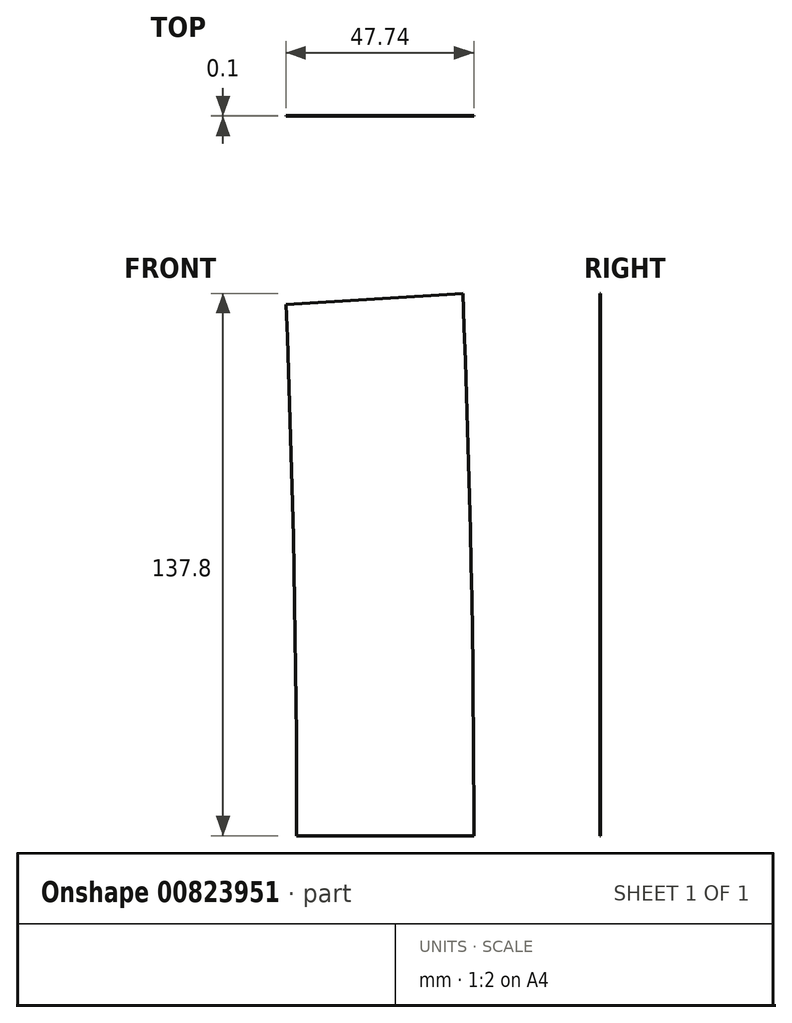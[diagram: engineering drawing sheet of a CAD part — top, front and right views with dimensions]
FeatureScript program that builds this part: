
annotation { "Feature Type Name" : "Feature", "Feature Type Description" : "" }
export const myFeature = defineFeature(function(context is Context, id is Id, definition is map)
    precondition{}
    {
        {
            var Q0;
            Q0=qCreatedBy(makeId("Front.planeOp"),FACE);
            var sketch = newSketch(context, id + "F0", { "sketchPlane" : qUnion([Q0])});
            skLineSegment(sketch, "E0", {"start": v(-45, 0) * mm, "end": v(0, 0) * mm});
            skLineSegment(sketch, "E1", {"start": v(-47.74, 134.96) * mm, "end": v(-2.83, 137.8) * mm});
            skArc(sketch, "E2", {"start": v(0, 0) * mm, "mid": v(-0.7, 68.92) * mm, "end": v(-2.83, 137.8) * mm});
            skArc(sketch, "E3", {"start": v(-45, 0) * mm, "mid": v(-45.68, 67.5) * mm, "end": v(-47.74, 134.96) * mm});
            skLineSegment(sketch, "E4", {"start": v(-2181.63, 0) * mm, "end": v(-2.83, 137.8) * mm, "construction": true});
            skSolve(sketch);
        }
        {
            var Q0;
            Q0=makeQuery(id+"F0.imprint","IMPRINT",FACE,{"disambiguationData":[TD([[makeQuery(id+"F0.imprint","IMPRINT",EDGE,{"derivedFrom":sQuery(id+"F0.wireOp",EDGE,"E0")}),1.0]])]});
            extrude(context, id + "F1", {"entities" : qUnion([Q0]), "depth" : 0.1 * mm, "offsetDistance" : 25 * mm});
        }
    });
